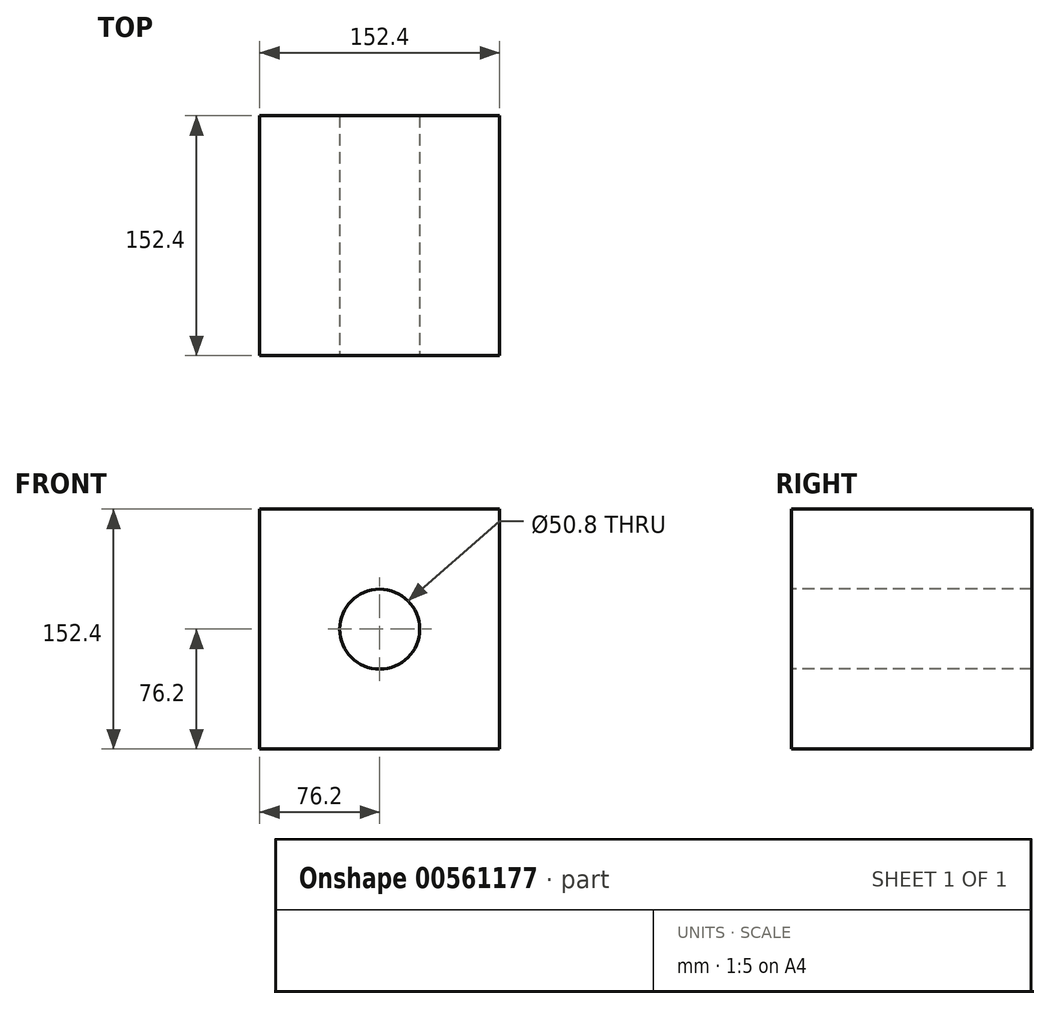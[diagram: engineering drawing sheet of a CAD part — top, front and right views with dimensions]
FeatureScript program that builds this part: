
annotation { "Feature Type Name" : "Feature", "Feature Type Description" : "" }
export const myFeature = defineFeature(function(context is Context, id is Id, definition is map)
    precondition{}
    {
        {
            var Q0;
            Q0=qCreatedBy(makeId("Front.planeOp"),FACE);
            var sketch = newSketch(context, id + "F0", { "sketchPlane" : qUnion([Q0])});
            skLineSegment(sketch, "E0.bottom", {"start": v(76.2, 76.2) * mm, "end": v(-76.2, 76.2) * mm});
            skLineSegment(sketch, "E0.top", {"start": v(76.2, -76.2) * mm, "end": v(-76.2, -76.2) * mm});
            skLineSegment(sketch, "E0.left", {"start": v(76.2, 76.2) * mm, "end": v(76.2, -76.2) * mm});
            skLineSegment(sketch, "E0.right", {"start": v(-76.2, 76.2) * mm, "end": v(-76.2, -76.2) * mm});
            skPoint(sketch, "E0.middle", {"position": v(0, 0) * mm});
            skSolve(sketch);
        }
        {
            var Q0;
            Q0 = qSketchRegion(id + "F0", true);
            extrude(context, id + "F1", {"entities" : qUnion([Q0]), "depth" : 152.4 * mm, "offsetDistance" : 25.4 * mm});
        }
        {
            var Q0;
            Q0=makeQuery(id+"F1.opExtrude","CAP_FACE",FACE,{"disambiguationData":[OSD([sQuery(id+"F0.wireOp",EDGE,"E0.bottom"),sQuery(id+"F0.wireOp",EDGE,"E0.top"),sQuery(id+"F0.wireOp",EDGE,"E0.left"),sQuery(id+"F0.wireOp",EDGE,"E0.right")])],"isStart":false});
            var sketch = newSketch(context, id + "F2", { "sketchPlane" : qUnion([Q0])});
            skCircle(sketch, "E1", {"center": v(0, 0) * mm, "radius": 25.4 * mm});
            skSolve(sketch);
        }
        {
            var Q0;
            Q0=makeQuery(id+"F2.imprint","IMPRINT",FACE,{"disambiguationData":[TD([[makeQuery(id+"F2.imprint","IMPRINT",EDGE,{"derivedFrom":sQuery(id+"F2.wireOp",EDGE,"E1")}),1.0]])]});
            extrude(context, id + "F3", {"entities" : qUnion([Q0]), "operationType" : NewBodyOperationType.REMOVE, "oppositeDirection" : true, "depth" : 152.4 * mm, "offsetDistance" : 25.4 * mm});
        }
    });
